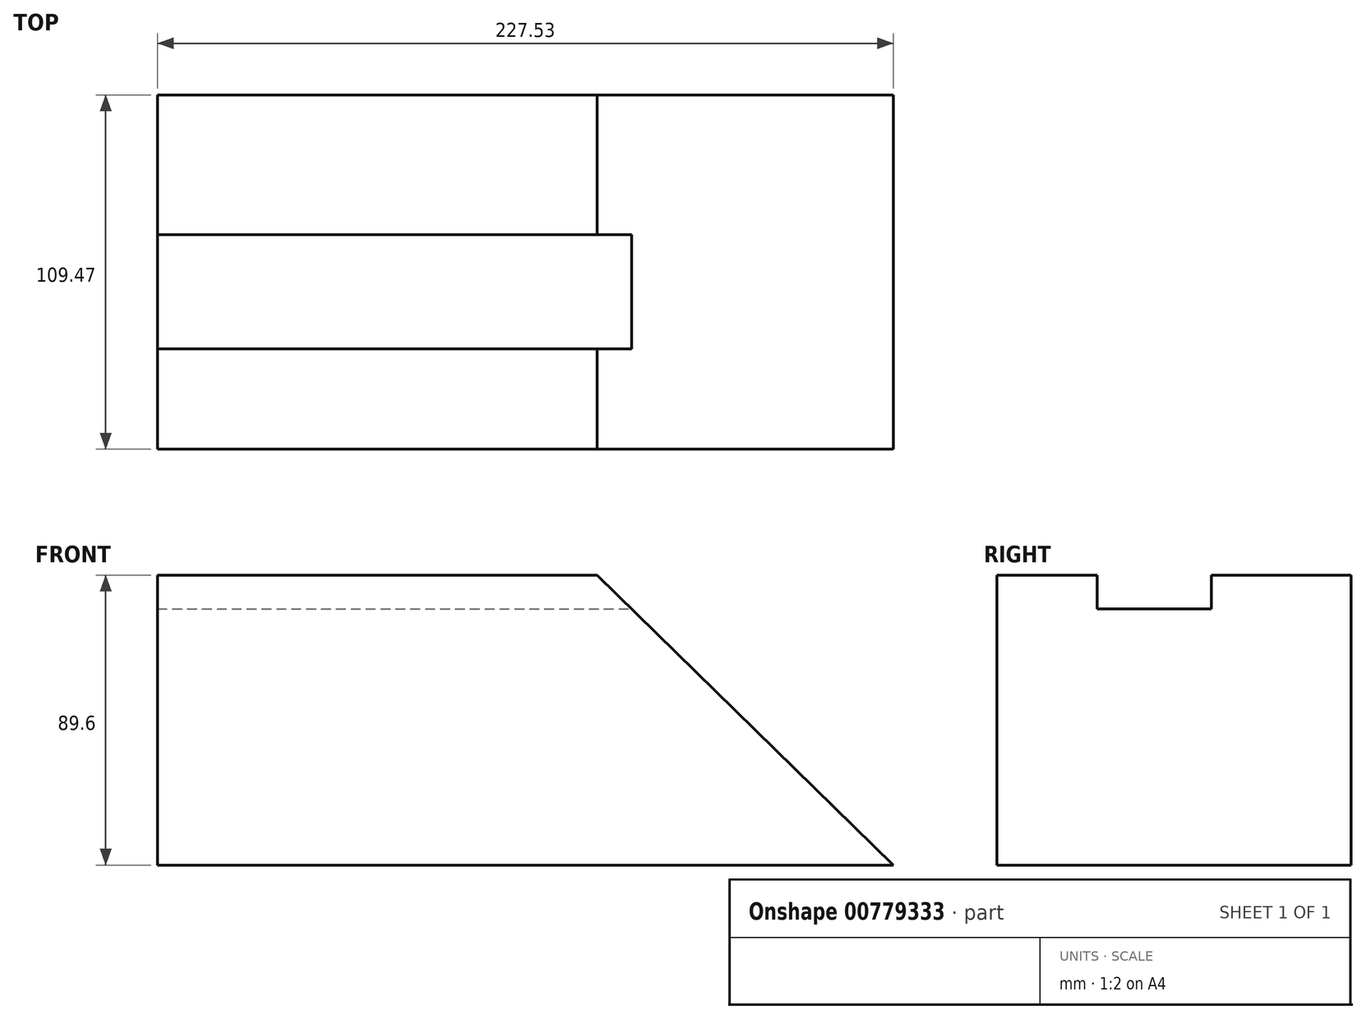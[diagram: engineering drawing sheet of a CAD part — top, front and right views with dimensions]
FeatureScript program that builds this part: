
annotation { "Feature Type Name" : "Feature", "Feature Type Description" : "" }
export const myFeature = defineFeature(function(context is Context, id is Id, definition is map)
    precondition{}
    {
        {
            var Q0;
            Q0=qCreatedBy(makeId("Front.planeOp"),FACE);
            var sketch = newSketch(context, id + "F0", { "sketchPlane" : qUnion([Q0])});
            skLineSegment(sketch, "E0.bottom", {"start": v(-94.19, 52.8) * mm, "end": v(98.75, 52.8) * mm});
            skLineSegment(sketch, "E0.top", {"start": v(-94.19, -36.8) * mm, "end": v(98.75, -36.8) * mm});
            skLineSegment(sketch, "E0.left", {"start": v(-94.19, 52.8) * mm, "end": v(-94.19, -36.8) * mm});
            skLineSegment(sketch, "E0.right", {"start": v(98.75, 52.8) * mm, "end": v(98.75, -36.8) * mm});
            skSolve(sketch);
        }
        {
            var Q0;
            Q0=makeQuery(id+"F0.imprint","IMPRINT",FACE,{"disambiguationData":[TD([[makeQuery(id+"F0.imprint","IMPRINT",EDGE,{"derivedFrom":sQuery(id+"F0.wireOp",EDGE,"E0.bottom")}),-1.0]])]});
            extrude(context, id + "F1", {"entities" : qUnion([Q0]), "depth" : 109.47 * mm, "offsetDistance" : 25.4 * mm});
        }
        {
            var Q0;
            Q0=qCreatedBy(makeId("Front.planeOp"),FACE);
            var sketch = newSketch(context, id + "F2", { "sketchPlane" : qUnion([Q0])});
            skLineSegment(sketch, "E1", {"start": v(99.07, -37.94) * mm, "end": v(0, 58.93) * mm});
            skLineSegment(sketch, "E2", {"start": v(0, 58.93) * mm, "end": v(95.09, 58.93) * mm});
            skLineSegment(sketch, "E3", {"start": v(95.09, 58.93) * mm, "end": v(122.37, 39.62) * mm});
            skLineSegment(sketch, "E4", {"start": v(122.37, 39.62) * mm, "end": v(122.37, -39.47) * mm});
            skLineSegment(sketch, "E5", {"start": v(122.37, -39.47) * mm, "end": v(99.07, -37.94) * mm});
            skSolve(sketch);
        }
        {
            var Q0;
            Q0=makeQuery(id+"F2.imprint","IMPRINT",FACE,{"disambiguationData":[TD([[makeQuery(id+"F2.imprint","IMPRINT",EDGE,{"derivedFrom":sQuery(id+"F2.wireOp",EDGE,"E1")}),-1.0]])]});
            extrude(context, id + "F3", {"entities" : qUnion([Q0]), "operationType" : NewBodyOperationType.REMOVE, "endBound" : BoundingType.SYMMETRIC, "depth" : 294.64 * mm, "offsetDistance" : 25.4 * mm});
        }
        {
            var Q0;
            Q0=makeQuery(id+"F1.opExtrude","SWEPT_FACE",FACE,{"disambiguationData":[OSD([sQuery(id+"F0.wireOp",EDGE,"E0.left")])]});
            extrude(context, id + "F4", {"entities" : qUnion([Q0]), "operationType" : NewBodyOperationType.ADD, "depth" : 85.6 * mm, "offsetDistance" : 25.4 * mm});
        }
        {
            var Q0;
            Q0=qCreatedBy(makeId("Right.planeOp"),FACE);
            var sketch = newSketch(context, id + "F5", { "sketchPlane" : qUnion([Q0])});
            skLineSegment(sketch, "E6.bottom", {"start": v(-43.23, 59.24) * mm, "end": v(-78.48, 59.24) * mm});
            skLineSegment(sketch, "E6.top", {"start": v(-43.23, 42.38) * mm, "end": v(-78.48, 42.38) * mm});
            skLineSegment(sketch, "E6.left", {"start": v(-43.23, 59.24) * mm, "end": v(-43.23, 42.38) * mm});
            skLineSegment(sketch, "E6.right", {"start": v(-78.48, 59.24) * mm, "end": v(-78.48, 42.38) * mm});
            skSolve(sketch);
        }
        {
            var Q0;
            Q0=makeQuery(id+"F5.imprint","IMPRINT",FACE,{"disambiguationData":[TD([[makeQuery(id+"F5.imprint","IMPRINT",EDGE,{"derivedFrom":sQuery(id+"F5.wireOp",EDGE,"E6.bottom")}),1.0]])]});
            extrude(context, id + "F6", {"entities" : qUnion([Q0]), "operationType" : NewBodyOperationType.REMOVE, "endBound" : BoundingType.SYMMETRIC, "oppositeDirection" : true, "depth" : 399.8 * mm, "offsetDistance" : 25.4 * mm});
        }
        {
            var Q0;
            Q0=qCreatedBy(makeId("Front.planeOp"),FACE);
            var sketch = newSketch(context, id + "F7", { "sketchPlane" : qUnion([Q0])});
            skLineSegment(sketch, "E7", {"start": v(-129.6, 68.13) * mm, "end": v(-129.6, -57.86) * mm});
            skLineSegment(sketch, "E8", {"start": v(-129.6, -57.86) * mm, "end": v(-195.51, -57.86) * mm});
            skLineSegment(sketch, "E9", {"start": v(-195.51, -57.86) * mm, "end": v(-195.51, 67.21) * mm});
            skLineSegment(sketch, "E10", {"start": v(-195.51, 67.21) * mm, "end": v(-129.6, 68.13) * mm});
            skSolve(sketch);
        }
        {
            var Q0;
            Q0=makeQuery(id+"F7.imprint","IMPRINT",FACE,{"disambiguationData":[TD([[makeQuery(id+"F7.imprint","IMPRINT",EDGE,{"derivedFrom":sQuery(id+"F7.wireOp",EDGE,"E7")}),-1.0]])]});
            extrude(context, id + "F8", {"entities" : qUnion([Q0]), "operationType" : NewBodyOperationType.REMOVE, "endBound" : BoundingType.SYMMETRIC, "depth" : 421.64 * mm, "offsetDistance" : 25.4 * mm});
        }
    });
